# Revit family: Clevertronics_LCWELED-HV-R_AUA01820060001
name_source: partatom
category: Lighting Fixtures
units: mm (PartAtom-declared; Revit-internal decimal feet)

## family parameters
Cut with Voids When Loaded = No
Host = Face
Light Source = Yes
Part Type = Normal
Room Calculation Point = No
Round Connector Dimension = Use Diameter
Shared = No

## types (1)
- Running Man Single
    Apparent Load = 5 VA
    Clevertronics_AS2293 Classification = C0=D8, C90=D6.3
    Clevertronics_Annotation Size = 0 mm  [stored 0 ft]
    Clevertronics_Applicable Standards = AS/NZS3820, CISPR15, AS/NZS2293.3
    Clevertronics_Battery = 3.3V 2500mAh
    Clevertronics_Battery Type = Lithium Nanophosphate
    Clevertronics_Charger Method = Intelligent Current Limited Constant Voltage
    Clevertronics_Construction = Polycarbonate white opal cover, glass reinforced nylon PA66 base
    Clevertronics_Diffuser = single sided running man(must specify diffuser combination)
    Clevertronics_Dimensions Main Enclosure = 410mm x 272mm x 100mm
    Clevertronics_Height = 100 mm  [stored 0.328084 ft]
    Clevertronics_IK Rating = IK10
    Clevertronics_IP Rating = IP66/IP67
    Clevertronics_Length = 410 mm  [stored 1.34514 ft]
    Clevertronics_MIC Number = AUA01820060001
    Clevertronics_Material = Clevertronics_Plastic
    Clevertronics_Mounting = Ceiling or Wall Mount, Single Sided
    Clevertronics_Operating Mode = Maintained
    Clevertronics_Operating Temperature = 0˚C to 40˚C
    Clevertronics_Operating Voltage = 240V AC; 50Hz
    Clevertronics_Power Consumption = 2.7 Watts (Standby), 5.1 Watts (Max)
    Clevertronics_Product Description = L10 Lithium Nanophosphate Classic Weatherproof Emergency EXIT, Single Sided, Zoneworks XT Hive
    Clevertronics_Replacement Battery = 1530010 : Battery
    Clevertronics_Replacement Driver = AUM01870310001 LCWELEDM-CKIT-HV-83 : Driver
    Clevertronics_Replacement Lamp = 8002430 : LED Strip
    Clevertronics_Testing Node = 8003191 : HV Node
    Clevertronics_Testing System = Zoneworks XT Hive
    Clevertronics_Viewing Distance = 24M
    Clevertronics_Weight = 1.9kg
    Clevertronics_Width = 272 mm
    Color Filter = 16777215
    Default Elevation = 1200 mm
    Description = L10 Lithium Nanophosphate Classic Weatherproof Emergency EXIT, Single Sided, Zoneworks XT Hive
    Dimming Lamp Color Temperature Shift = <None>
    Indication Left 'Face Two' = No
    Indication Left 'Face one' = No
    Indication Right 'Face Two' = No
    Indication Right 'Face one' = No
    Lamp = 6 x LED lamp bar assembly 100,000 hours
    Manufacturer = Clevertronics
    Model = LCWELED-HV-R
    Photometric Web File = LCWELED-ZW-DS-RAOW_IESA_E_CIE_LL21014_20180529.IES
    Runing Man common arrow = No
    Straight line 'Face one' = Yes
    Straight line 'Face two' = No
    Tilt Angle = -90.00°

note: [stored X ft] marks values corroborated as IEEE doubles in the binary element streams (Revit-internal decimal feet)

## geometry (parser evidence)
native form markers: Blend x2, Sweep x5
no freeform markers — native parametric forms only
